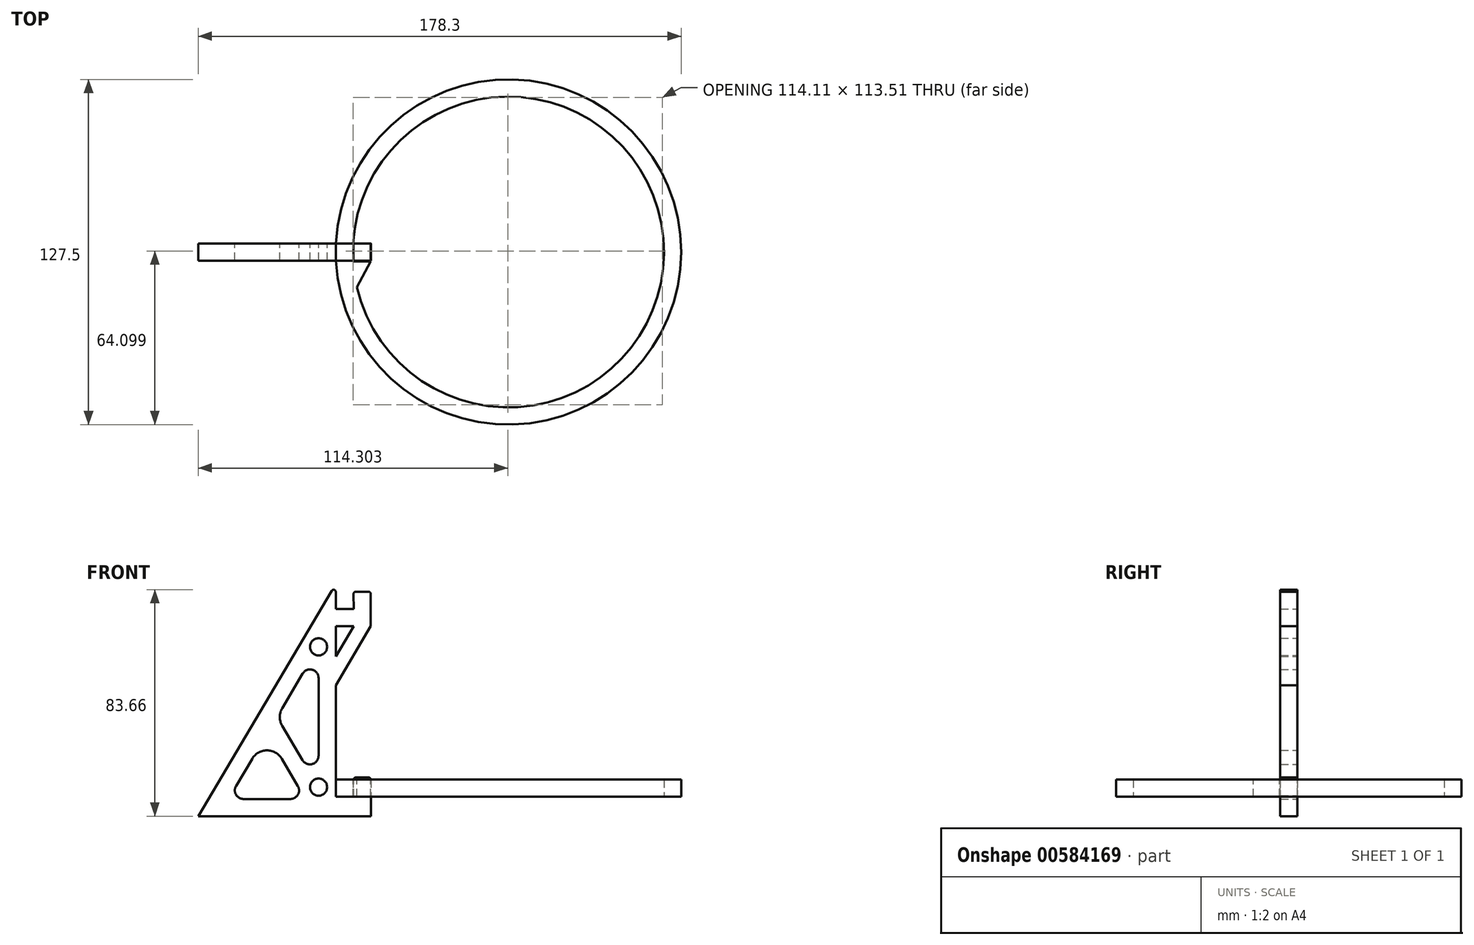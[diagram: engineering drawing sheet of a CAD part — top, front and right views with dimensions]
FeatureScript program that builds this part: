
annotation { "Feature Type Name" : "Feature", "Feature Type Description" : "" }
export const myFeature = defineFeature(function(context is Context, id is Id, definition is map)
    precondition{}
    {
        {
            var Q0;
            Q0=qCreatedBy(makeId("Front.planeOp"),FACE);
            var sketch = newSketch(context, id + "F0", { "sketchPlane" : qUnion([Q0])});
            skLineSegment(sketch, "E0", {"start": v(-63.75, 0) * mm, "end": v(-114.55, 0) * mm});
            skLineSegment(sketch, "E1", {"start": v(-114.55, 0) * mm, "end": v(-65.2, 83.27) * mm});
            skLineSegment(sketch, "E2", {"start": v(-63.75, 82.88) * mm, "end": v(-63.75, 76.56) * mm});
            skPoint(sketch, "E3.orphan", {"position": v(-89.15, 42.86) * mm});
            skLineSegment(sketch, "E4", {"start": v(-63.75, 0) * mm, "end": v(-57.15, 0) * mm});
            skLineSegment(sketch, "E5", {"start": v(-57.15, 7.13) * mm, "end": v(-57.15, 13.48) * mm});
            skLineSegment(sketch, "E6", {"start": v(-56.37, 14.26) * mm, "end": v(-51.58, 14.26) * mm});
            skLineSegment(sketch, "E7", {"start": v(-50.8, 13.48) * mm, "end": v(-50.8, 0) * mm});
            skLineSegment(sketch, "E8", {"start": v(-50.8, 0) * mm, "end": v(-50.8, 7.13) * mm});
            skLineSegment(sketch, "E9", {"start": v(-57.15, 7.13) * mm, "end": v(-63.75, 7.13) * mm});
            skLineSegment(sketch, "E10", {"start": v(-57.15, 0) * mm, "end": v(-50.8, 0) * mm});
            skLineSegment(sketch, "E11", {"start": v(-63.75, 70.2) * mm, "end": v(-57.12, 70.2) * mm});
            skLineSegment(sketch, "E12", {"start": v(-57.15, 76.56) * mm, "end": v(-57.18, 82.12) * mm});
            skLineSegment(sketch, "E13", {"start": v(-56.4, 82.9) * mm, "end": v(-51.61, 82.9) * mm});
            skLineSegment(sketch, "E14", {"start": v(-50.83, 82.12) * mm, "end": v(-50.83, 70.2) * mm});
            skLineSegment(sketch, "E15", {"start": v(-57.15, 76.56) * mm, "end": v(-63.75, 76.56) * mm});
            skLineSegment(sketch, "E16.0", {"start": v(-100.57, 11.14) * mm, "end": v(-94.62, 21.19) * mm});
            skLineSegment(sketch, "E16.1", {"start": v(-80.47, 6.35) * mm, "end": v(-97.84, 6.35) * mm});
            skLineSegment(sketch, "E16.2", {"start": v(-70.1, 51.06) * mm, "end": v(-70.1, 22.3) * mm});
            skLineSegment(sketch, "E17", {"start": v(-83.55, 33.4) * mm, "end": v(-76.01, 20.68) * mm});
            skLineSegment(sketch, "E18.0", {"start": v(-83.7, 21.19) * mm, "end": v(-77.74, 11.14) * mm});
            skLineSegment(sketch, "E19.trimOffspring", {"start": v(-83.55, 39.87) * mm, "end": v(-75.96, 52.67) * mm});
            skLineSegment(sketch, "E20.trimOffspring", {"start": v(-63.75, 70.2) * mm, "end": v(-63.75, 59) * mm});
            skLineSegment(sketch, "E21.0", {"start": v(-50.83, 70.2) * mm, "end": v(-63.75, 48.4) * mm});
            skLineSegment(sketch, "E22.0", {"start": v(-57.12, 70.2) * mm, "end": v(-63.75, 59) * mm});
            skLineSegment(sketch, "E23.trimOffspring", {"start": v(-63.75, 48.4) * mm, "end": v(-63.75, 7.13) * mm});
            skPoint(sketch, "E24.visualSharp", {"position": v(-63.75, 85.72) * mm});
            skArc(sketch, "E24.filletArc", {"start": v(-63.75, 82.88) * mm, "mid": v(-64.33, 83.63) * mm, "end": v(-65.2, 83.27) * mm});
            skPoint(sketch, "E25.visualSharp", {"position": v(-57.18, 82.9) * mm});
            skArc(sketch, "E25.filletArc", {"start": v(-56.4, 82.9) * mm, "mid": v(-56.95, 82.68) * mm, "end": v(-57.18, 82.12) * mm});
            skPoint(sketch, "E26.visualSharp", {"position": v(-50.83, 82.9) * mm});
            skArc(sketch, "E26.filletArc", {"start": v(-50.83, 82.12) * mm, "mid": v(-51.06, 82.68) * mm, "end": v(-51.61, 82.9) * mm});
            skPoint(sketch, "E27.visualSharp", {"position": v(-63.75, 76.56) * mm});
            skLineSegment(sketch, "E27.filletArc", {"start": v(-63.75, 76.56) * mm, "end": v(-63.75, 76.56) * mm});
            skPoint(sketch, "E28.visualSharp", {"position": v(-57.15, 76.56) * mm});
            skLineSegment(sketch, "E28.filletArc", {"start": v(-57.15, 76.56) * mm, "end": v(-57.15, 76.56) * mm});
            skPoint(sketch, "E29.visualSharp", {"position": v(-57.15, 14.26) * mm});
            skArc(sketch, "E29.filletArc", {"start": v(-56.37, 14.26) * mm, "mid": v(-56.92, 14.03) * mm, "end": v(-57.15, 13.48) * mm});
            skPoint(sketch, "E30.visualSharp", {"position": v(-50.8, 14.26) * mm});
            skArc(sketch, "E30.filletArc", {"start": v(-50.8, 13.48) * mm, "mid": v(-51.03, 14.03) * mm, "end": v(-51.58, 14.26) * mm});
            skPoint(sketch, "E31.visualSharp", {"position": v(-85.46, 36.63) * mm});
            skArc(sketch, "E31.filletArc", {"start": v(-83.55, 39.87) * mm, "mid": v(-84.43, 36.63) * mm, "end": v(-83.55, 33.4) * mm});
            skPoint(sketch, "E32.visualSharp", {"position": v(-89.15, 30.4) * mm});
            skArc(sketch, "E32.filletArc", {"start": v(-83.7, 21.19) * mm, "mid": v(-89.15, 24.3) * mm, "end": v(-94.62, 21.19) * mm});
            skPoint(sketch, "E33.visualSharp", {"position": v(-74.9, 6.35) * mm});
            skArc(sketch, "E33.filletArc", {"start": v(-80.47, 6.35) * mm, "mid": v(-77.71, 7.95) * mm, "end": v(-77.74, 11.14) * mm});
            skPoint(sketch, "E34.visualSharp", {"position": v(-103.4, 6.35) * mm});
            skArc(sketch, "E34.filletArc", {"start": v(-100.57, 11.14) * mm, "mid": v(-100.6, 7.95) * mm, "end": v(-97.84, 6.35) * mm});
            skPoint(sketch, "E35.visualSharp", {"position": v(-70.1, 10.72) * mm});
            skArc(sketch, "E35.filletArc", {"start": v(-76.01, 20.68) * mm, "mid": v(-72.44, 19.24) * mm, "end": v(-70.1, 22.3) * mm});
            skPoint(sketch, "E36.visualSharp", {"position": v(-70.1, 62.55) * mm});
            skArc(sketch, "E36.filletArc", {"start": v(-70.1, 51.06) * mm, "mid": v(-72.42, 54.1) * mm, "end": v(-75.96, 52.67) * mm});
            skCircle(sketch, "E37", {"center": v(-70.1, 62.55) * mm, "radius": 3.18 * mm});
            skCircle(sketch, "E38", {"center": v(-70.1, 10.72) * mm, "radius": 3.18 * mm});
            skLineSegment(sketch, "E39.filletArc", {"start": v(-57.15, 7.13) * mm, "end": v(-57.15, 7.13) * mm});
            skLineSegment(sketch, "E40.filletArc", {"start": v(-63.75, 7.13) * mm, "end": v(-63.75, 7.13) * mm});
            skSolve(sketch);
        }
        {
            var Q0;
            Q0 = qSketchRegion(id + "F0", true);
            extrude(context, id + "F1", {"entities" : qUnion([Q0]), "endBound" : BoundingType.SYMMETRIC, "depth" : 6.35 * mm, "offsetDistance" : 25.4 * mm});
        }
        {
            var Q0;
            Q0=makeQuery(id+"F1.opExtrude","SWEPT_FACE",FACE,{"disambiguationData":[OSD([sQuery(id+"F0.wireOp",EDGE,"E9")])]});
            var sketch = newSketch(context, id + "F2", { "sketchPlane" : qUnion([Q0])});
            skCircle(sketch, "E41", {"center": v(0, 0) * mm, "radius": 63.75 * mm});
            skCircle(sketch, "E42.0", {"center": v(0, 0) * mm, "radius": 57.4 * mm});
            skSolve(sketch);
        }
        {
            var Q0;
            {var subQ0=sQuery(id+"F2.wireOp",EDGE,"E41");var subQ1=sQuery(id+"F0.wireOp",EDGE,"E9");var subQ2=makeQuery(id+"F1.opExtrude","CAP_EDGE",EDGE,{"disambiguationData":[OSD([subQ1])],"isStart":true});var subQ3=makeQuery(id+"F2.imprint","INTERSECT",VERTEX,{"derivedFrom":[subQ2,subQ0]});Q0=makeQuery(id+"F2.imprint","IMPRINT",FACE,{"disambiguationData":[TD([[makeQuery(id+"F2.imprint","IMPRINT",EDGE,{"disambiguationData":[TD([[subQ3,1.0]])],"derivedFrom":subQ0}),1.0]])]});}
            var Q1;
            {var subQ0=sQuery(id+"F2.wireOp",EDGE,"E42.0");var subQ1=sQuery(id+"F0.wireOp",EDGE,"E9");var subQ2=makeQuery(id+"F1.opExtrude","CAP_EDGE",EDGE,{"disambiguationData":[OSD([subQ1])],"isStart":true});var subQ3=makeQuery(id+"F2.imprint","INTERSECT",VERTEX,{"derivedFrom":[subQ2,subQ0]});Q1=makeQuery(id+"F2.imprint","IMPRINT",FACE,{"disambiguationData":[TD([[makeQuery(id+"F2.imprint","IMPRINT",EDGE,{"disambiguationData":[TD([[subQ3,-1.0]])],"derivedFrom":subQ0}),-1.0]])]});}
            extrude(context, id + "F3", {"entities" : qUnion([Q0, Q1]), "depth" : 6.35 * mm, "offsetDistance" : 25.4 * mm});
        }
        {
            var Q0;
            Q0=makeQuery(id+"F3.opExtrude","CAP_FACE",FACE,{"disambiguationData":[OSD([sQuery(id+"F2.wireOp",EDGE,"bF2BX4Xj-wiJE-2XbZ-gde7-i5PxY7a12vhl"),sQuery(id+"F2.wireOp",EDGE,"E41")])],"isStart":false});
            var sketch = newSketch(context, id + "F4", { "sketchPlane" : qUnion([Q0])});
            skSolve(sketch);
        }
        {
            var Q0;
            Q0=makeQuery(id+"F4.imprint","IMPRINT",FACE,{"disambiguationData":[TD([[makeQuery(id+"F4.imprint","IMPRINT",EDGE,{"derivedFrom":makeQuery(id+"F3.opExtrude","CAP_EDGE",EDGE,{"disambiguationData":[OSD([sQuery(id+"F2.wireOp",EDGE,"E41")])],"isStart":false})}),1.0]])]});
            var sketch = newSketch(context, id + "F5", { "sketchPlane" : qUnion([Q0])});
            skPoint(sketch, "E43.0", {"position": v(-50.8, -3.18) * mm});
            skArc(sketch, "E44.0", {"start": v(-57.3, -3.43) * mm, "mid": v(-56.8, -8.26) * mm, "end": v(-55.9, -13.03) * mm});
            skLineSegment(sketch, "E45", {"start": v(-50.93, -3.43) * mm, "end": v(-55.9, -13.03) * mm});
            skLineSegment(sketch, "E46.0", {"start": v(-50.93, -3.43) * mm, "end": v(-57.3, -3.43) * mm});
            skSolve(sketch);
        }
        {
            var Q0;
            Q0 = qSketchRegion(id + "F5", true);
            var Q1;
            Q1=makeQuery(id+"F3.opExtrude","CAP_FACE",FACE,{"disambiguationData":[OSD([sQuery(id+"F2.wireOp",EDGE,"E41"),sQuery(id+"F2.wireOp",EDGE,"E42.0")])],"isStart":true});
            extrude(context, id + "F6", {"entities" : qUnion([Q0]), "operationType" : NewBodyOperationType.ADD, "endBound" : BoundingType.UP_TO_SURFACE, "oppositeDirection" : true, "depth" : 25.4 * mm, "endBoundEntityFace" : qUnion([Q1]), "offsetDistance" : 25.4 * mm});
        }
    });
